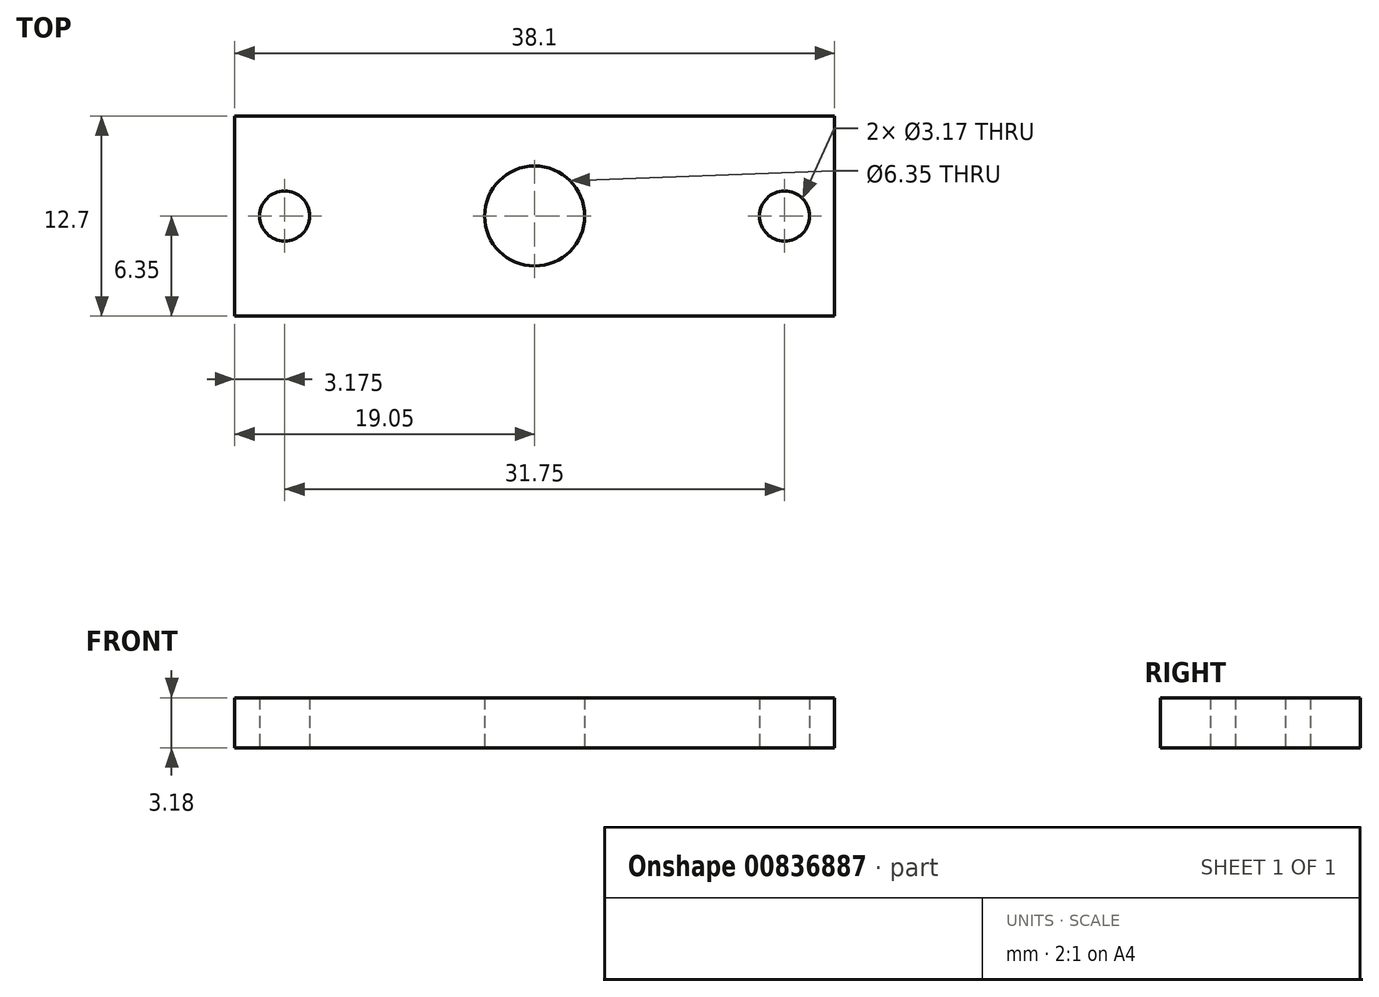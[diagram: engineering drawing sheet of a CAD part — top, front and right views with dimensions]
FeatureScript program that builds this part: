
annotation { "Feature Type Name" : "Feature", "Feature Type Description" : "" }
export const myFeature = defineFeature(function(context is Context, id is Id, definition is map)
    precondition{}
    {
        {
            var Q0;
            Q0=qCreatedBy(makeId("Top.planeOp"),FACE);
            var sketch = newSketch(context, id + "F0", { "sketchPlane" : qUnion([Q0])});
            skLineSegment(sketch, "E0.bottom", {"start": v(0, 0) * mm, "end": v(38.1, 0) * mm});
            skLineSegment(sketch, "E0.top", {"start": v(0, 12.7) * mm, "end": v(38.1, 12.7) * mm});
            skLineSegment(sketch, "E0.left", {"start": v(0, 0) * mm, "end": v(0, 12.7) * mm});
            skLineSegment(sketch, "E0.right", {"start": v(38.1, 0) * mm, "end": v(38.1, 12.7) * mm});
            skCircle(sketch, "E1", {"center": v(3.18, 6.35) * mm, "radius": 1.59 * mm});
            skPoint(sketch, "E1.centerSnap0", {"position": v(0, 6.35) * mm});
            skCircle(sketch, "E2", {"center": v(34.92, 6.35) * mm, "radius": 1.59 * mm});
            skLineSegment(sketch, "E3", {"start": v(0, 6.35) * mm, "end": v(3.18, 6.35) * mm, "construction": true});
            skLineSegment(sketch, "E4", {"start": v(34.92, 6.35) * mm, "end": v(38.1, 6.35) * mm, "construction": true});
            skCircle(sketch, "E5", {"center": v(19.05, 6.35) * mm, "radius": 3.18 * mm});
            skLineSegment(sketch, "E6", {"start": v(3.17, 6.35) * mm, "end": v(19.05, 6.35) * mm, "construction": true});
            skLineSegment(sketch, "E7", {"start": v(34.92, 6.35) * mm, "end": v(19.05, 6.35) * mm, "construction": true});
            skSolve(sketch);
        }
        {
            var Q0;
            Q0 = qSketchRegion(id + "F0", true);
            extrude(context, id + "F1", {"entities" : qUnion([Q0]), "depth" : 3.17 * mm, "offsetDistance" : 25.4 * mm});
        }
    });
